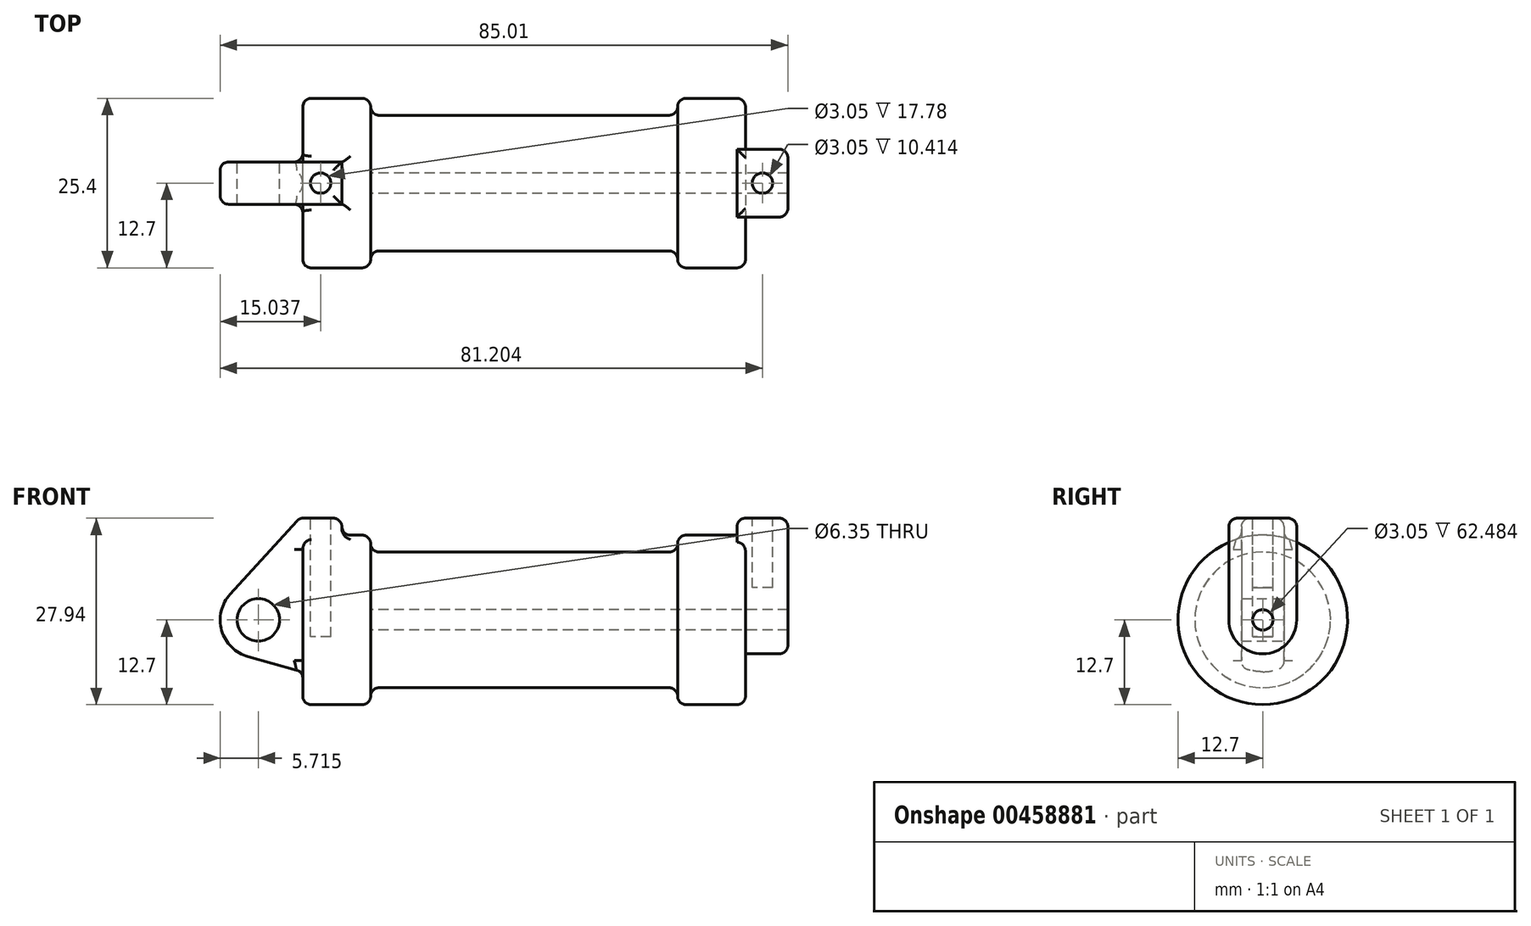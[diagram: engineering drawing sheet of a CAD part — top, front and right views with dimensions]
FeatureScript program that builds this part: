
annotation { "Feature Type Name" : "Feature", "Feature Type Description" : "" }
export const myFeature = defineFeature(function(context is Context, id is Id, definition is map)
    precondition{}
    {
        {
            var Q0;
            Q0=qCreatedBy(makeId("Front.planeOp"),FACE);
            var sketch = newSketch(context, id + "F0", { "sketchPlane" : qUnion([Q0])});
            skLineSegment(sketch, "E0", {"start": v(0, 0) * mm, "end": v(0, 12.7) * mm});
            skLineSegment(sketch, "E1", {"start": v(0, 12.7) * mm, "end": v(10.16, 12.7) * mm});
            skLineSegment(sketch, "E2", {"start": v(10.16, 12.7) * mm, "end": v(10.16, 10.16) * mm});
            skLineSegment(sketch, "E3", {"start": v(10.16, 10.16) * mm, "end": v(56.13, 10.16) * mm});
            skLineSegment(sketch, "E4", {"start": v(56.13, 10.16) * mm, "end": v(56.13, 12.7) * mm});
            skLineSegment(sketch, "E5", {"start": v(56.13, 12.7) * mm, "end": v(66.3, 12.7) * mm});
            skLineSegment(sketch, "E6", {"start": v(66.3, 12.7) * mm, "end": v(66.3, 0) * mm});
            skLineSegment(sketch, "E7", {"start": v(66.3, 0) * mm, "end": v(0, 0) * mm});
            skLineSegment(sketch, "E8", {"start": v(5.84, 15.24) * mm, "end": v(-0.5, 15.24) * mm});
            skLineSegment(sketch, "E9", {"start": v(-0.5, 15.24) * mm, "end": v(-10.88, 3.85) * mm});
            skLineSegment(sketch, "E10", {"start": v(0, 0) * mm, "end": v(-6.65, 0) * mm});
            skCircle(sketch, "E11", {"center": v(-6.65, 0) * mm, "radius": 5.72 * mm});
            skCircle(sketch, "E12", {"center": v(-6.65, 0) * mm, "radius": 3.18 * mm});
            skLineSegment(sketch, "E13", {"start": v(5.84, 15.24) * mm, "end": v(5.84, -9.4) * mm});
            skLineSegment(sketch, "E14", {"start": v(5.84, -9.4) * mm, "end": v(-8.18, -5.5) * mm});
            skSolve(sketch);
        }
        {
            var Q0;
            {var subQ0=sQuery(id+"F0.wireOp",EDGE,"E2");Q0=makeQuery(id+"F0.imprint","IMPRINT",FACE,{"disambiguationData":[TD([[makeQuery(id+"F0.imprint","IMPRINT",EDGE,{"derivedFrom":subQ0}),-1.0]])]});}
            var Q1;
            {var subQ0=sQuery(id+"F0.wireOp",EDGE,"E0");Q1=makeQuery(id+"F0.imprint","IMPRINT",FACE,{"disambiguationData":[TD([[makeQuery(id+"F0.imprint","IMPRINT",EDGE,{"derivedFrom":subQ0}),-1.0]])]});}
            var Q2;
            Q2=sQuery(id+"F0.wireOp",EDGE,"E7");
            revolve(context, id + "F1", {"entities" : qUnion([Q0, Q1]), "axis" : qUnion([Q2]), "revolveType" : RevolveType.FULL});
        }
        {
            var Q0;
            {var subQ0=sQuery(id+"F0.wireOp",EDGE,"E0");Q0=makeQuery(id+"F0.imprint","IMPRINT",FACE,{"disambiguationData":[TD([[makeQuery(id+"F0.imprint","IMPRINT",EDGE,{"derivedFrom":subQ0}),-1.0]])]});}
            var Q1;
            {var subQ1=sQuery(id+"F0.wireOp",EDGE,"E0");Q1=makeQuery(id+"F0.imprint","IMPRINT",FACE,{"disambiguationData":[TD([[makeQuery(id+"F0.imprint","IMPRINT",EDGE,{"derivedFrom":subQ1}),1.0]])]});}
            var Q2;
            {var subQ0=sQuery(id+"F0.wireOp",EDGE,"E14");Q2=makeQuery(id+"F0.imprint","IMPRINT",FACE,{"disambiguationData":[TD([[makeQuery(id+"F0.imprint","IMPRINT",EDGE,{"derivedFrom":subQ0}),-1.0]])]});}
            var Q3;
            {var subQ5=sQuery(id+"F0.wireOp",EDGE,"E12");Q3=makeQuery(id+"F0.imprint","IMPRINT",FACE,{"disambiguationData":[TD([[makeQuery(id+"F0.imprint","IMPRINT",EDGE,{"derivedFrom":subQ5}),-1.0]])]});}
            extrude(context, id + "F2", {"entities" : qUnion([Q0, Q1, Q2, Q3]), "operationType" : NewBodyOperationType.ADD, "depth" : 6.35 * mm, "symmetric" : true});
        }
        {
            var Q0;
            Q0=makeQuery(id+"F1.opRevolve","SWEPT_FACE",FACE,{"disambiguationData":[OSD([sQuery(id+"F0.wireOp",EDGE,"E6")])]});
            var sketch = newSketch(context, id + "F3", { "sketchPlane" : qUnion([Q0])});
            skCircle(sketch, "E15", {"center": v(0, 0) * mm, "radius": 1.52 * mm});
            skCircle(sketch, "E16", {"center": v(0, 0) * mm, "radius": 5.08 * mm});
            skLineSegment(sketch, "E17", {"start": v(5.08, 0) * mm, "end": v(5.08, 15.24) * mm});
            skLineSegment(sketch, "E18", {"start": v(-5.08, 0) * mm, "end": v(-5.08, 15.24) * mm});
            skLineSegment(sketch, "E19", {"start": v(-5.08, 15.24) * mm, "end": v(5.08, 15.24) * mm});
            skSolve(sketch);
        }
        {
            var Q0;
            Q0=makeQuery(id+"F2.opExtrude","SWEPT_FACE",FACE,{"disambiguationData":[OSD([sQuery(id+"F0.wireOp",EDGE,"E8")])]});
            var sketch = newSketch(context, id + "F4", { "sketchPlane" : qUnion([Q0])});
            skCircle(sketch, "E20", {"center": v(2.67, 0) * mm, "radius": 1.52 * mm});
            skSolve(sketch);
        }
        {
            var Q0;
            Q0 = qSketchRegion(id + "F4", true);
            extrude(context, id + "F5", {"entities" : qUnion([Q0]), "operationType" : NewBodyOperationType.REMOVE, "oppositeDirection" : true, "depth" : 17.78 * mm});
        }
        {
            var Q0;
            {var subQ0=sQuery(id+"F3.wireOp",EDGE,"E19");Q0=makeQuery(id+"F3.imprint","IMPRINT",FACE,{"disambiguationData":[TD([[makeQuery(id+"F3.imprint","IMPRINT",EDGE,{"derivedFrom":subQ0}),-1.0]])]});}
            extrude(context, id + "F6", {"entities" : qUnion([Q0]), "operationType" : NewBodyOperationType.ADD, "oppositeDirection" : true, "depth" : 1.27 * mm});
        }
        {
            var Q0;
            {var subQ0=sQuery(id+"F3.wireOp",EDGE,"E17");var subQ1=sQuery(id+"F3.wireOp",EDGE,"E16");var subQ2=makeQuery(id+"F3.imprint","INTERSECT",VERTEX,{"derivedFrom":[subQ1,subQ0]});Q0=makeQuery(id+"F3.imprint","IMPRINT",FACE,{"disambiguationData":[TD([[makeQuery(id+"F3.imprint","IMPRINT",EDGE,{"disambiguationData":[TD([[subQ2,-1.0]])],"derivedFrom":subQ1}),-1.0]])]});}
            var Q1;
            Q1=makeQuery(id+"F3.imprint","IMPRINT",FACE,{"disambiguationData":[TD([[makeQuery(id+"F3.imprint","IMPRINT",EDGE,{"derivedFrom":sQuery(id+"F3.wireOp",EDGE,"E15")}),-1.0]])]});
            var Q2;
            {var subQ0=sQuery(id+"F3.wireOp",EDGE,"E19");Q2=makeQuery(id+"F3.imprint","IMPRINT",FACE,{"disambiguationData":[TD([[makeQuery(id+"F3.imprint","IMPRINT",EDGE,{"derivedFrom":subQ0}),-1.0]])]});}
            extrude(context, id + "F7", {"entities" : qUnion([Q0, Q1, Q2]), "operationType" : NewBodyOperationType.ADD, "depth" : 6.35 * mm});
        }
        {
            var Q0;
            Q0=makeQuery(id+"F3.imprint","IMPRINT",FACE,{"disambiguationData":[TD([[makeQuery(id+"F3.imprint","IMPRINT",EDGE,{"derivedFrom":sQuery(id+"F3.wireOp",EDGE,"E15")}),1.0]])]});
            var Q1;
            Q1=makeQuery(id+"F1.opRevolve","SWEPT_FACE",FACE,{"disambiguationData":[OSD([sQuery(id+"F0.wireOp",EDGE,"E2")])]});
            extrude(context, id + "F8", {"entities" : qUnion([Q0]), "operationType" : NewBodyOperationType.REMOVE, "endBound" : BoundingType.UP_TO_SURFACE, "oppositeDirection" : true, "endBoundEntityFace" : qUnion([Q1]), "depth" : 25.4 * mm});
        }
        {
            var Q0;
            {var subQ0=sQuery(id+"F3.wireOp",EDGE,"E19");Q0=makeQuery(id+"F7.boolean.opBoolean","MERGE",FACE,{"derivedFrom":[makeQuery(id+"F6.opExtrude","SWEPT_FACE",FACE,{"disambiguationData":[OSD([subQ0])]}),makeQuery(id+"F7.opExtrude","SWEPT_FACE",FACE,{"disambiguationData":[OSD([subQ0])]})]});}
            var sketch = newSketch(context, id + "F9", { "sketchPlane" : qUnion([Q0])});
            skLineSegment(sketch, "E21", {"start": v(68.83, 5.08) * mm, "end": v(68.83, -5.08) * mm, "construction": true});
            skLineSegment(sketch, "E22", {"start": v(72.64, 0) * mm, "end": v(65.02, 0) * mm, "construction": true});
            skCircle(sketch, "E23", {"center": v(68.83, 0) * mm, "radius": 1.52 * mm});
            skSolve(sketch);
        }
        {
            var Q0;
            Q0=makeQuery(id+"F9.imprint","IMPRINT",FACE,{"disambiguationData":[TD([[makeQuery(id+"F9.imprint","IMPRINT",EDGE,{"derivedFrom":sQuery(id+"F9.wireOp",EDGE,"E23")}),1.0]])]});
            extrude(context, id + "F10", {"entities" : qUnion([Q0]), "operationType" : NewBodyOperationType.REMOVE, "oppositeDirection" : true, "depth" : 10.4 * mm});
        }
        {
            var Q0;
            Q0=makeQuery(id+"F1.opRevolve","SWEPT_EDGE",EDGE,{"disambiguationData":[OSD([sQuery(id+"F0.wireOp",EDGE,"E1"),sQuery(id+"F0.wireOp",EDGE,"E2")])]});
            var Q1;
            Q1=makeQuery(id+"F1.opRevolve","SWEPT_EDGE",EDGE,{"disambiguationData":[OSD([sQuery(id+"F0.wireOp",EDGE,"E4"),sQuery(id+"F0.wireOp",EDGE,"E5")])]});
            var Q2;
            Q2=makeQuery(id+"F1.opRevolve","SWEPT_EDGE",EDGE,{"disambiguationData":[OSD([sQuery(id+"F0.wireOp",EDGE,"E0"),sQuery(id+"F0.wireOp",EDGE,"E1")])]});
            var Q3;
            Q3=makeQuery(id+"F1.opRevolve","SWEPT_EDGE",EDGE,{"disambiguationData":[OSD([sQuery(id+"F0.wireOp",EDGE,"E5"),sQuery(id+"F0.wireOp",EDGE,"E6")])]});
            var Q4;
            Q4=makeQuery(id+"F1.opRevolve","SWEPT_EDGE",EDGE,{"disambiguationData":[OSD([sQuery(id+"F0.wireOp",EDGE,"E2"),sQuery(id+"F0.wireOp",EDGE,"E3")])]});
            var Q5;
            Q5=makeQuery(id+"F1.opRevolve","SWEPT_EDGE",EDGE,{"disambiguationData":[OSD([sQuery(id+"F0.wireOp",EDGE,"E3"),sQuery(id+"F0.wireOp",EDGE,"E4")])]});
            fillet(context, id + "F11", {"entities" : qUnion([Q0, Q1, Q2, Q3, Q4, Q5]), "radius" : 1.27 * mm, "tangentPropagation" : true, "allowEdgeOverflow" : false});
        }
        {
            var Q0;
            Q0=makeQuery(id+"F2.opExtrude","CAP_EDGE",EDGE,{"disambiguationData":[OSD([sQuery(id+"F0.wireOp",EDGE,"E8")])],"isStart":true});
            var Q1;
            Q1=makeQuery(id+"F2.opExtrude","SWEPT_EDGE",EDGE,{"disambiguationData":[OSD([sQuery(id+"F0.wireOp",EDGE,"E8"),sQuery(id+"F0.wireOp",EDGE,"E9")])]});
            var Q2;
            Q2=makeQuery(id+"F2.opExtrude","SWEPT_EDGE",EDGE,{"disambiguationData":[OSD([sQuery(id+"F0.wireOp",EDGE,"E8"),sQuery(id+"F0.wireOp",EDGE,"E13")])]});
            var Q3;
            Q3=makeQuery(id+"F2.opExtrude","CAP_EDGE",EDGE,{"disambiguationData":[OSD([sQuery(id+"F0.wireOp",EDGE,"E8")])],"isStart":false});
            var Q4;
            Q4=makeQuery(id+"F2.boolean.opBoolean","INTERSECT",EDGE,{"derivedFrom":[makeQuery(id+"F1.opRevolve","SWEPT_FACE",FACE,{"disambiguationData":[OSD([sQuery(id+"F0.wireOp",EDGE,"E1")])]}),makeQuery(id+"F2.opExtrude","SWEPT_FACE",FACE,{"disambiguationData":[OSD([sQuery(id+"F0.wireOp",EDGE,"E13")])]})]});
            var Q5;
            Q5=makeQuery(id+"F2.boolean.opBoolean","INTERSECT",EDGE,{"derivedFrom":[makeQuery(id+"F1.opRevolve","SWEPT_FACE",FACE,{"disambiguationData":[OSD([sQuery(id+"F0.wireOp",EDGE,"E1")])]}),makeQuery(id+"F2.opExtrude","CAP_FACE",FACE,{"disambiguationData":[OSD([sQuery(id+"F0.wireOp",EDGE,"E8"),sQuery(id+"F0.wireOp",EDGE,"E9"),sQuery(id+"F0.wireOp",EDGE,"E11"),sQuery(id+"F0.wireOp",EDGE,"E12"),sQuery(id+"F0.wireOp",EDGE,"E13"),sQuery(id+"F0.wireOp",EDGE,"E14")])],"isStart":false})]});
            var Q6;
            {var subQ0=sQuery(id+"F0.wireOp",EDGE,"E1");Q6=makeQuery(id+"F11.opFillet","BLEND_EDGE",EDGE,{"blendedFrom":[makeQuery(id+"F1.opRevolve","SWEPT_EDGE",EDGE,{"disambiguationData":[OSD([sQuery(id+"F0.wireOp",EDGE,"E0"),subQ0])]}),makeQuery(id+"F1.opRevolve","SWEPT_FACE",FACE,{"disambiguationData":[OSD([subQ0])]})],"blendedInto":[makeQuery(id+"F1.opRevolve","SWEPT_FACE",FACE,{"disambiguationData":[OSD([subQ0])]})]});}
            var Q7;
            Q7=makeQuery(id+"F2.boolean.opBoolean","INTERSECT",EDGE,{"derivedFrom":[makeQuery(id+"F1.opRevolve","SWEPT_FACE",FACE,{"disambiguationData":[OSD([sQuery(id+"F0.wireOp",EDGE,"E1")])]}),makeQuery(id+"F2.opExtrude","CAP_FACE",FACE,{"disambiguationData":[OSD([sQuery(id+"F0.wireOp",EDGE,"E8"),sQuery(id+"F0.wireOp",EDGE,"E9"),sQuery(id+"F0.wireOp",EDGE,"E11"),sQuery(id+"F0.wireOp",EDGE,"E12"),sQuery(id+"F0.wireOp",EDGE,"E13"),sQuery(id+"F0.wireOp",EDGE,"E14")])],"isStart":true})]});
            var Q8;
            Q8=makeQuery(id+"F2.opExtrude","CAP_EDGE",EDGE,{"disambiguationData":[OSD([sQuery(id+"F0.wireOp",EDGE,"E9")])],"isStart":true});
            var Q9;
            Q9=makeQuery(id+"F2.opExtrude","CAP_EDGE",EDGE,{"disambiguationData":[OSD([sQuery(id+"F0.wireOp",EDGE,"E9")])],"isStart":false});
            var Q10;
            Q10=makeQuery(id+"F7.opExtrude","CAP_EDGE",EDGE,{"disambiguationData":[OSD([sQuery(id+"F3.wireOp",EDGE,"E17")])],"isStart":false});
            var Q11;
            Q11=makeQuery(id+"F7.opExtrude","CAP_EDGE",EDGE,{"disambiguationData":[OSD([sQuery(id+"F3.wireOp",EDGE,"E18")])],"isStart":false});
            var Q12;
            Q12=makeQuery(id+"F7.opExtrude","CAP_EDGE",EDGE,{"disambiguationData":[OSD([sQuery(id+"F3.wireOp",EDGE,"E19")])],"isStart":false});
            var Q13;
            {var subQ0=sQuery(id+"F3.wireOp",EDGE,"E19");var subQ1=sQuery(id+"F3.wireOp",EDGE,"E18");Q13=makeQuery(id+"F7.boolean.opBoolean","MERGE",EDGE,{"derivedFrom":[makeQuery(id+"F6.opExtrude","SWEPT_EDGE",EDGE,{"disambiguationData":[OSD([subQ1,subQ0])]}),makeQuery(id+"F7.opExtrude","SWEPT_EDGE",EDGE,{"disambiguationData":[OSD([subQ1,subQ0])]})]});}
            var Q14;
            {var subQ0=sQuery(id+"F3.wireOp",EDGE,"E19");var subQ1=sQuery(id+"F3.wireOp",EDGE,"E17");Q14=makeQuery(id+"F7.boolean.opBoolean","MERGE",EDGE,{"derivedFrom":[makeQuery(id+"F6.opExtrude","SWEPT_EDGE",EDGE,{"disambiguationData":[OSD([subQ1,subQ0])]}),makeQuery(id+"F7.opExtrude","SWEPT_EDGE",EDGE,{"disambiguationData":[OSD([subQ1,subQ0])]})]});}
            var Q15;
            Q15=makeQuery(id+"F6.opExtrude","CAP_EDGE",EDGE,{"disambiguationData":[OSD([sQuery(id+"F0.wireOp",EDGE,"E5"),sQuery(id+"F0.wireOp",EDGE,"E6")])],"isStart":false});
            var Q16;
            Q16=makeQuery(id+"F6.opExtrude","CAP_EDGE",EDGE,{"disambiguationData":[OSD([sQuery(id+"F3.wireOp",EDGE,"E19")])],"isStart":false});
            var Q17;
            Q17=makeQuery(id+"F7.opExtrude","CAP_EDGE",EDGE,{"disambiguationData":[OSD([sQuery(id+"F3.wireOp",EDGE,"E18")])],"isStart":true});
            var Q18;
            Q18=makeQuery(id+"F7.opExtrude","CAP_EDGE",EDGE,{"disambiguationData":[OSD([sQuery(id+"F3.wireOp",EDGE,"E16")])],"isStart":true});
            var Q19;
            Q19=makeQuery(id+"F7.opExtrude","CAP_EDGE",EDGE,{"disambiguationData":[OSD([sQuery(id+"F3.wireOp",EDGE,"E17")])],"isStart":true});
            fillet(context, id + "F12", {"entities" : qUnion([Q0, Q1, Q2, Q3, Q4, Q5, Q6, Q7, Q8, Q9, Q10, Q11, Q12, Q13, Q14, Q15, Q16, Q17, Q18, Q19]), "radius" : 1.27 * mm, "tangentPropagation" : true, "allowEdgeOverflow" : false});
        }
    });
